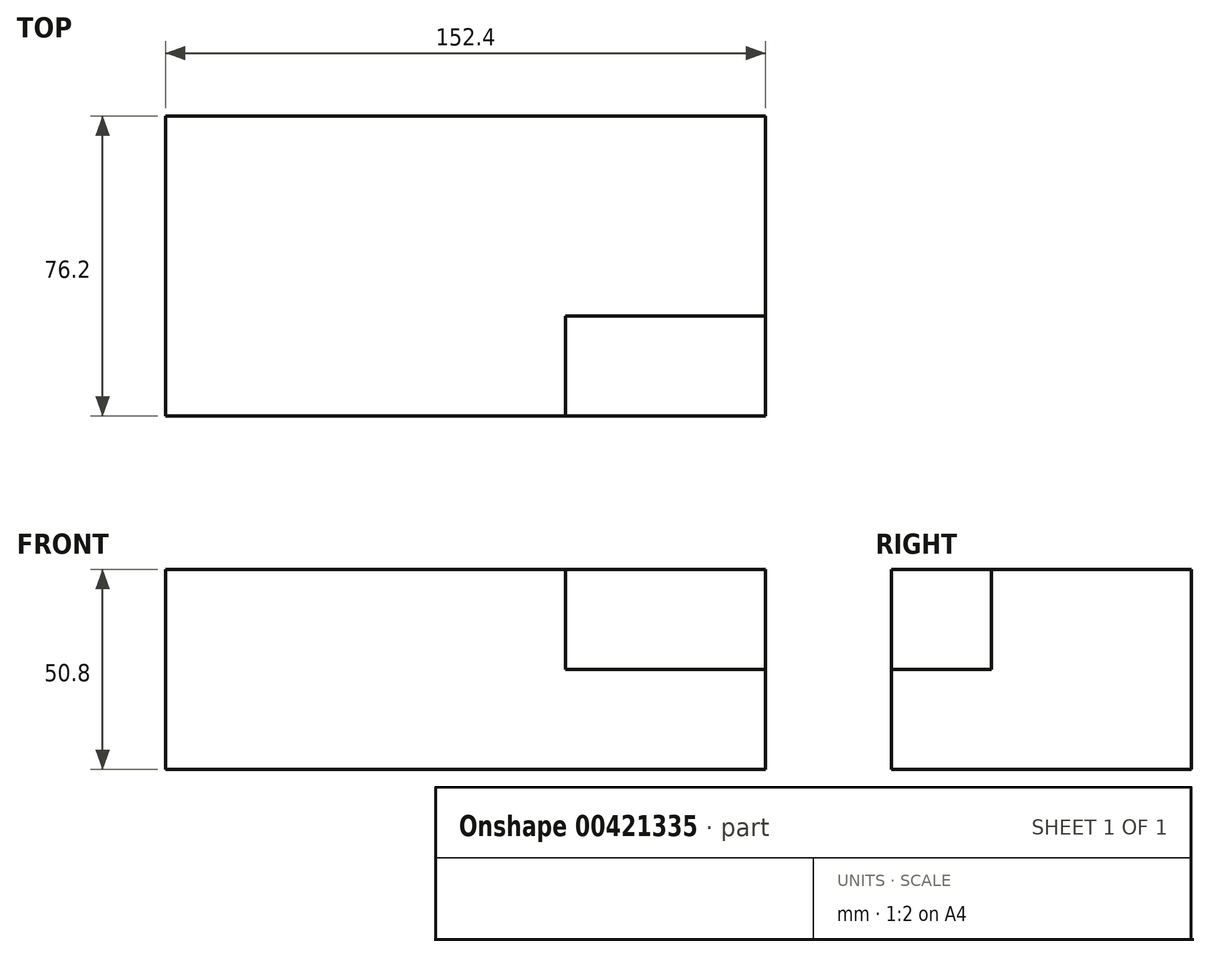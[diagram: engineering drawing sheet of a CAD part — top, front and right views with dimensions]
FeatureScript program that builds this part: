
annotation { "Feature Type Name" : "Feature", "Feature Type Description" : "" }
export const myFeature = defineFeature(function(context is Context, id is Id, definition is map)
    precondition{}
    {
        {
            var Q0;
            Q0=qCreatedBy(makeId("Right.planeOp"),FACE);
            var sketch = newSketch(context, id + "F0", { "sketchPlane" : qUnion([Q0])});
            skLineSegment(sketch, "E0", {"start": v(0, 0) * mm, "end": v(76.2, 0) * mm});
            skLineSegment(sketch, "E1", {"start": v(76.2, 0) * mm, "end": v(76.2, 50.8) * mm});
            skLineSegment(sketch, "E2", {"start": v(0, 0) * mm, "end": v(0, 25.4) * mm});
            skLineSegment(sketch, "E3", {"start": v(0, 25.4) * mm, "end": v(25.4, 25.4) * mm});
            skLineSegment(sketch, "E4", {"start": v(25.4, 25.4) * mm, "end": v(25.4, 50.8) * mm});
            skLineSegment(sketch, "E5", {"start": v(25.4, 50.8) * mm, "end": v(76.2, 50.8) * mm});
            skLineSegment(sketch, "E6", {"start": v(0, 25.4) * mm, "end": v(0, 50.8) * mm});
            skLineSegment(sketch, "E7", {"start": v(0, 50.8) * mm, "end": v(25.4, 50.8) * mm});
            skSolve(sketch);
        }
        {
            var Q0;
            Q0=makeQuery(id+"F0.imprint","IMPRINT",FACE,{"disambiguationData":[TD([[makeQuery(id+"F0.imprint","IMPRINT",EDGE,{"derivedFrom":sQuery(id+"F0.wireOp",EDGE,"E0")}),1.0]])]});
            var Q1;
            Q1=makeQuery(id+"F0.imprint","IMPRINT",FACE,{"disambiguationData":[TD([[makeQuery(id+"F0.imprint","IMPRINT",EDGE,{"derivedFrom":sQuery(id+"F0.wireOp",EDGE,"E3")}),1.0]])]});
            extrude(context, id + "F1", {"entities" : qUnion([Q0, Q1]), "depth" : 152.4 * mm});
        }
        {
            var Q0;
            Q0=makeQuery(id+"F1.opExtrude","SWEPT_FACE",FACE,{"disambiguationData":[OSD([sQuery(id+"F0.wireOp",EDGE,"E5"),sQuery(id+"F0.wireOp",EDGE,"E7")])]});
            var sketch = newSketch(context, id + "F2", { "sketchPlane" : qUnion([Q0])});
            skSolve(sketch);
        }
        {
            var Q0;
            {var subQ0=sQuery(id+"F0.wireOp",EDGE,"E5");Q0=makeQuery(id+"F2.imprint","IMPRINT",FACE,{"disambiguationData":[TD([[makeQuery(id+"F2.imprint","IMPRINT",EDGE,{"derivedFrom":makeQuery(id+"F1.opExtrude","SWEPT_EDGE",EDGE,{"disambiguationData":[OSD([sQuery(id+"F0.wireOp",EDGE,"E1"),subQ0])]})}),1.0]])]});}
            var sketch = newSketch(context, id + "F3", { "sketchPlane" : qUnion([Q0])});
            skLineSegment(sketch, "E8", {"start": v(0, 0) * mm, "end": v(101.6, 0) * mm});
            skLineSegment(sketch, "E9", {"start": v(101.6, 0) * mm, "end": v(152.4, 0) * mm});
            skLineSegment(sketch, "E10", {"start": v(0, 0) * mm, "end": v(0, 76.2) * mm});
            skLineSegment(sketch, "E11", {"start": v(0, 76.2) * mm, "end": v(152.4, 76.2) * mm});
            skLineSegment(sketch, "E12", {"start": v(152.4, 76.2) * mm, "end": v(152.4, 0) * mm});
            skLineSegment(sketch, "E13", {"start": v(101.6, 0) * mm, "end": v(101.6, 25.4) * mm});
            skLineSegment(sketch, "E14", {"start": v(101.6, 25.4) * mm, "end": v(152.4, 25.4) * mm});
            skSolve(sketch);
        }
        {
            var Q0;
            {var subQ0=sQuery(id+"F3.wireOp",EDGE,"E9");Q0=makeQuery(id+"F3.imprint","IMPRINT",FACE,{"disambiguationData":[TD([[makeQuery(id+"F3.imprint","IMPRINT",EDGE,{"derivedFrom":subQ0}),-1.0]])]});}
            extrude(context, id + "F4", {"entities" : qUnion([Q0]), "operationType" : NewBodyOperationType.REMOVE, "oppositeDirection" : true, "depth" : 25.4 * mm});
        }
    });
